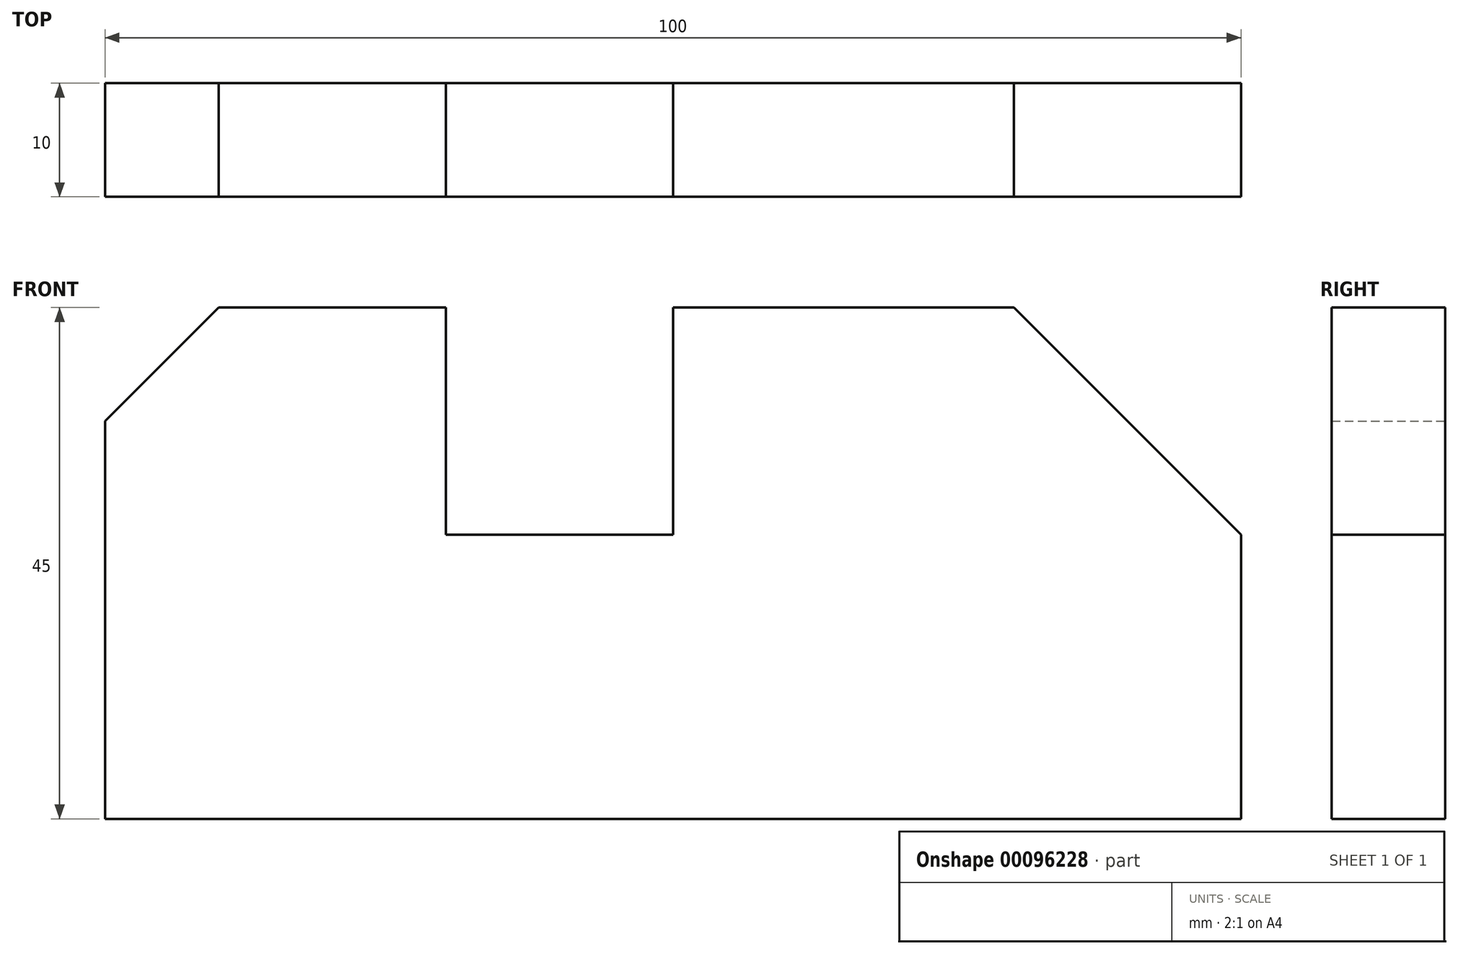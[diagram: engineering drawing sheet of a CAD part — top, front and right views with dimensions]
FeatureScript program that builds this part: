
annotation { "Feature Type Name" : "Feature", "Feature Type Description" : "" }
export const myFeature = defineFeature(function(context is Context, id is Id, definition is map)
    precondition{}
    {
        {
            var Q0;
            Q0=qCreatedBy(makeId("Front.planeOp"),FACE);
            var sketch = newSketch(context, id + "F0", { "sketchPlane" : qUnion([Q0])});
            skLineSegment(sketch, "E0", {"start": v(0, 0) * mm, "end": v(100, 0) * mm});
            skLineSegment(sketch, "E1", {"start": v(100, 0) * mm, "end": v(100, 25) * mm});
            skLineSegment(sketch, "E2", {"start": v(100, 25) * mm, "end": v(80, 45) * mm});
            skLineSegment(sketch, "E3", {"start": v(80, 45) * mm, "end": v(50, 45) * mm});
            skLineSegment(sketch, "E4", {"start": v(50, 45) * mm, "end": v(50, 25) * mm});
            skLineSegment(sketch, "E5", {"start": v(50, 25) * mm, "end": v(30, 25) * mm});
            skLineSegment(sketch, "E6", {"start": v(30, 25) * mm, "end": v(30, 45) * mm});
            skLineSegment(sketch, "E7", {"start": v(30, 45) * mm, "end": v(10, 45) * mm});
            skLineSegment(sketch, "E8", {"start": v(10, 45) * mm, "end": v(0, 35) * mm});
            skLineSegment(sketch, "E9", {"start": v(0, 35) * mm, "end": v(0, 0) * mm});
            skLineSegment(sketch, "E10", {"start": v(30, 45) * mm, "end": v(50, 45) * mm, "construction": true});
            skSolve(sketch);
        }
        {
            var Q0;
            Q0 = qSketchRegion(id + "F0", true);
            extrude(context, id + "F1", {"entities" : qUnion([Q0]), "depth" : 10 * mm});
        }
    });
